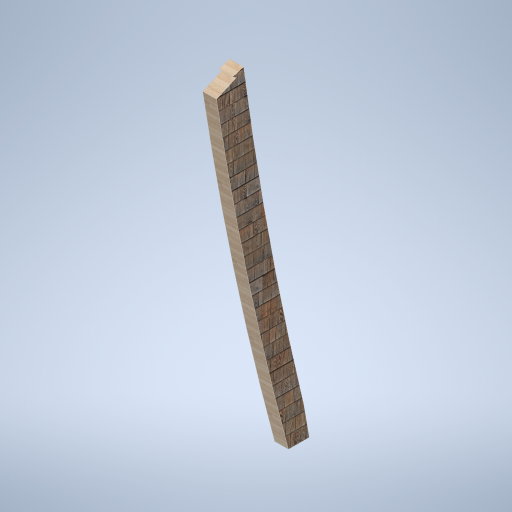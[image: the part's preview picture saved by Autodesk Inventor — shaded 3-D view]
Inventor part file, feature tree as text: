
AUTODESK INVENTOR PART (.ipt)
format: ipt  version: 2024.2 (Build 282272000, 272)  size: 315,392 bytes
history: native  units: mm
features: extrude x1, sketch x1
ambient origin geometry x8: Origin, YZ Plane, XZ Plane, XY Plane, X Axis, Y Axis, Z Axis, Center Point
bodies: Solid1 (feature_tree)
feature tree (2):
  extrude  "Extrusion1"  Depth=40000.0mm
  sketch  "Sketch1"  dims[d0=40000.0mm d1=40000.0mm d2=400.0mm d3=175.0mm d4=0.0mm]
